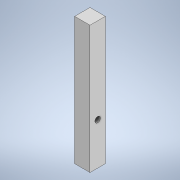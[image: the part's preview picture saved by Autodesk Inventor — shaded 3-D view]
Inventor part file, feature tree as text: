
AUTODESK INVENTOR PART (.ipt)
format: ipt  version: 2020.2 (Build 242310000, 310)  size: 102,400 bytes
history: native  units: mm
features: sketch x2, extrude x1, hole x1
ambient origin geometry x8: Origin, YZ Plane, XZ Plane, XY Plane, X Axis, Y Axis, Z Axis, Center Point
bodies: Solid1 (feature_tree)
feature tree (4):
  extrude  "Extrusion1"  Depth=83.2mm
  hole  "Hole1"  [1 undecoded]
  sketch  "Sketch1"  dims[d0=10.0mm d1=83.2mm]
  sketch  "Sketch2"  dims[d2=10.0mm d3=0.0mm d4=55.8mm d5=3.6mm d6=6.0mm d7=6.3mm d8=2.0mm d9=90.0deg d10=8.0mm d11=0.0mm]
note: 1 required parameter value undecoded (feature->parameter linkage not recoverable at this tier; creation-order binding heuristic only, values carry confidence <= 0.55)
